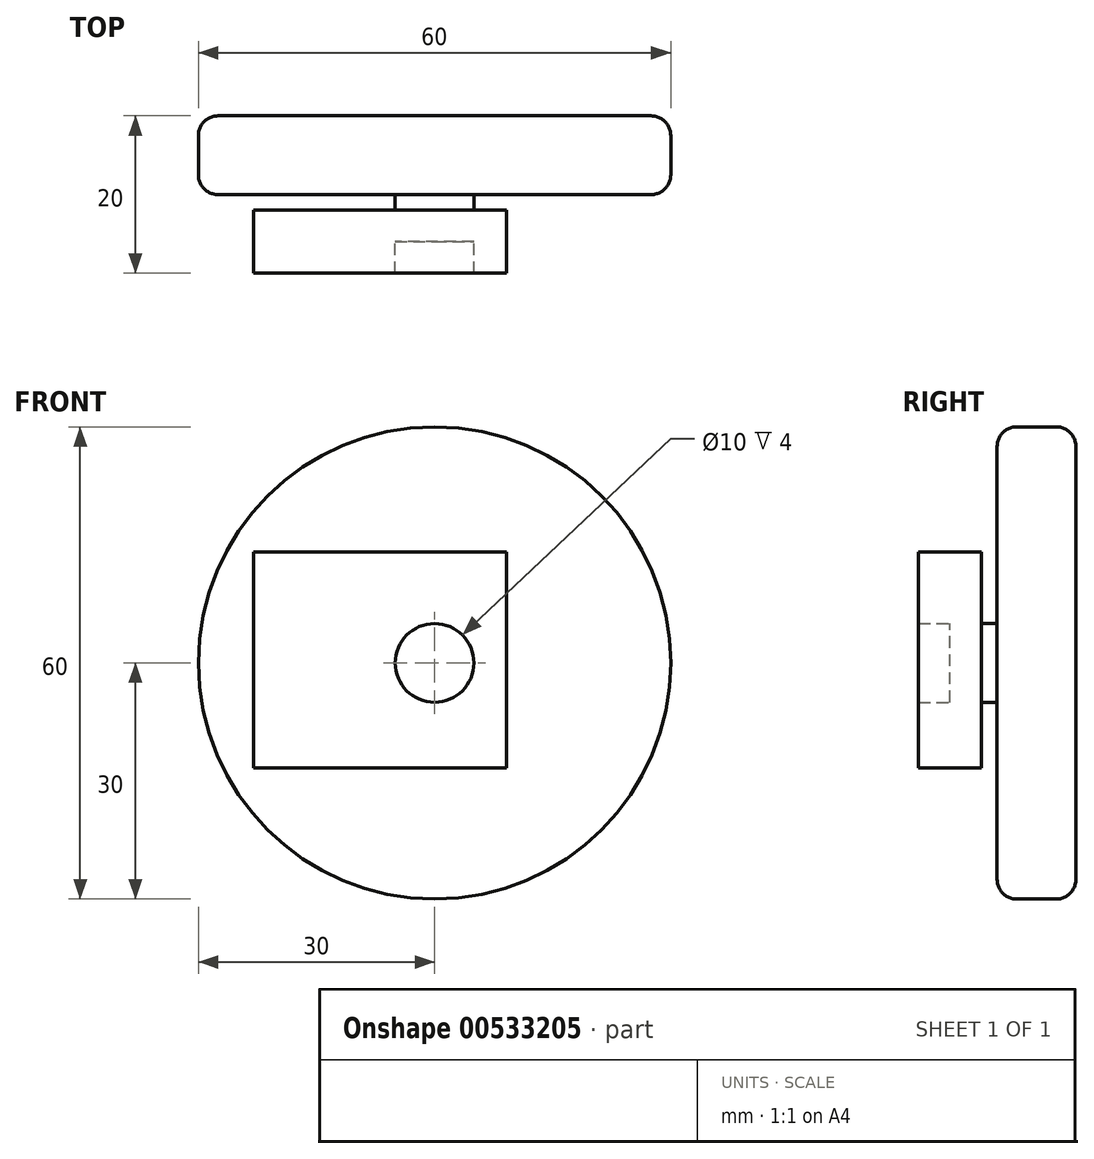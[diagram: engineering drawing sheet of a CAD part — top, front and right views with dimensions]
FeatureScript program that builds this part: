
annotation { "Feature Type Name" : "Feature", "Feature Type Description" : "" }
export const myFeature = defineFeature(function(context is Context, id is Id, definition is map)
    precondition{}
    {
        {
            var Q0;
            Q0=qCreatedBy(makeId("Front.planeOp"),FACE);
            var sketch = newSketch(context, id + "F0", { "sketchPlane" : qUnion([Q0])});
            skCircle(sketch, "E0", {"center": v(0, 0) * mm, "radius": 30 * mm});
            skSolve(sketch);
        }
        {
            var Q0;
            Q0=makeQuery(id+"F0.imprint","IMPRINT",FACE,{"disambiguationData":[TD([[makeQuery(id+"F0.imprint","IMPRINT",EDGE,{"derivedFrom":sQuery(id+"F0.wireOp",EDGE,"E0")}),1.0]])]});
            extrude(context, id + "F1", {"entities" : qUnion([Q0]), "depth" : 10 * mm, "offsetDistance" : 25.4 * mm});
        }
        {
            var Q0;
            Q0=makeQuery(id+"F1.opExtrude","CAP_EDGE",EDGE,{"disambiguationData":[OSD([sQuery(id+"F0.wireOp",EDGE,"E0")])],"isStart":false});
            fillet(context, id + "F2", {"entities" : qUnion([Q0]), "radius" : 2.5 * mm, "tangentPropagation" : true, "allowEdgeOverflow" : false});
        }
        {
            var Q0;
            Q0=makeQuery(id+"F1.opExtrude","CAP_EDGE",EDGE,{"disambiguationData":[OSD([sQuery(id+"F0.wireOp",EDGE,"E0")])],"isStart":true});
            var Q1;
            {var subQ0=sQuery(id+"F0.wireOp",EDGE,"E0");Q1=makeQuery(id+"F2.opFillet","BLEND_EDGE",EDGE,{"blendedFrom":[makeQuery(id+"F1.opExtrude","CAP_EDGE",EDGE,{"disambiguationData":[OSD([subQ0])],"isStart":false}),makeQuery(id+"F1.opExtrude","CAP_FACE",FACE,{"disambiguationData":[OSD([subQ0])],"isStart":false})],"blendedInto":[makeQuery(id+"F1.opExtrude","CAP_FACE",FACE,{"disambiguationData":[OSD([subQ0])],"isStart":false})]});}
            fillet(context, id + "F3", {"entities" : qUnion([Q0, Q1]), "radius" : 2.5 * mm, "tangentPropagation" : true, "allowEdgeOverflow" : false});
        }
        {
            var Q0;
            Q0=makeQuery(id+"F1.opExtrude","CAP_FACE",FACE,{"disambiguationData":[OSD([sQuery(id+"F0.wireOp",EDGE,"E0")])],"isStart":false});
            var sketch = newSketch(context, id + "F4", { "sketchPlane" : qUnion([Q0])});
            skCircle(sketch, "E1", {"center": v(0, 0) * mm, "radius": 5 * mm});
            skSolve(sketch);
        }
        {
            var Q0;
            Q0 = qSketchRegion(id + "F4", true);
            extrude(context, id + "F5", {"entities" : qUnion([Q0]), "operationType" : NewBodyOperationType.ADD, "depth" : 6 * mm, "offsetDistance" : 25 * mm});
        }
        {
            var Q0;
            Q0=makeQuery(id+"F5.opExtrude","CAP_FACE",FACE,{"disambiguationData":[OSD([sQuery(id+"F4.wireOp",EDGE,"E1")])],"isStart":false});
            var sketch = newSketch(context, id + "F6", { "sketchPlane" : qUnion([Q0])});
            skLineSegment(sketch, "E2.bottom", {"start": v(-23, 14.1) * mm, "end": v(9.1, 14.1) * mm});
            skLineSegment(sketch, "E2.top", {"start": v(-23, -13.36) * mm, "end": v(9.1, -13.36) * mm});
            skLineSegment(sketch, "E2.left", {"start": v(-23, 14.1) * mm, "end": v(-23, -13.36) * mm});
            skLineSegment(sketch, "E2.right", {"start": v(9.1, 14.1) * mm, "end": v(9.1, -13.36) * mm});
            skSolve(sketch);
        }
        {
            var Q0;
            Q0=makeQuery(id+"F6.imprint","IMPRINT",FACE,{"disambiguationData":[TD([[makeQuery(id+"F6.imprint","IMPRINT",EDGE,{"derivedFrom":sQuery(id+"F6.wireOp",EDGE,"E2.bottom")}),-1.0]])]});
            extrude(context, id + "F7", {"entities" : qUnion([Q0]), "operationType" : NewBodyOperationType.ADD, "endBound" : BoundingType.SYMMETRIC, "depth" : 8 * mm, "offsetDistance" : 25 * mm});
        }
    });
